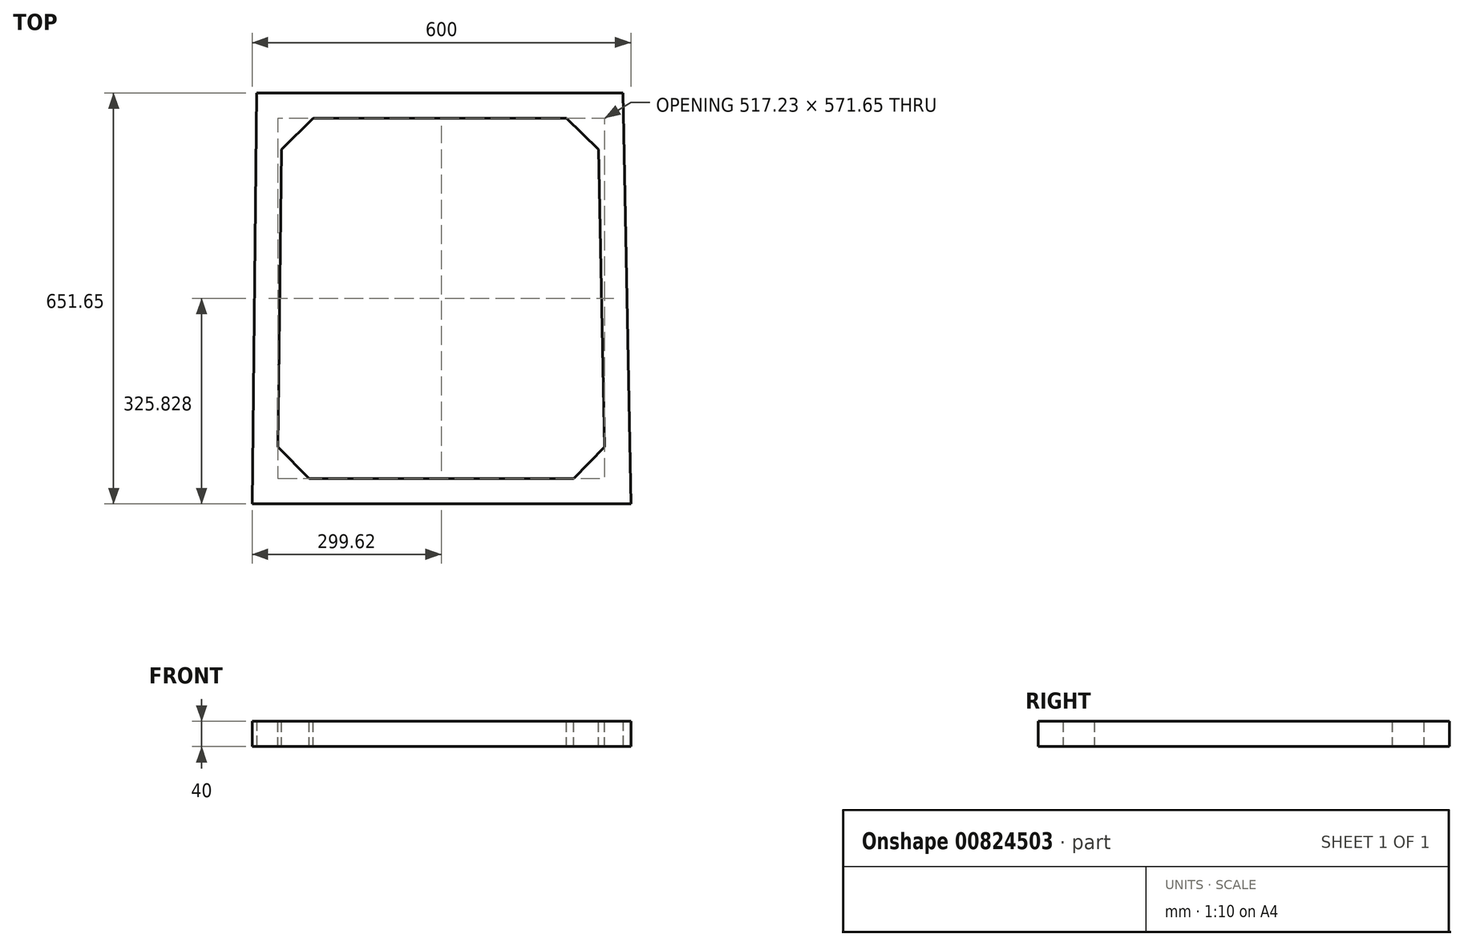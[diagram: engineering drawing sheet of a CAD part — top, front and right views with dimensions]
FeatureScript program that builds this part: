
annotation { "Feature Type Name" : "Feature", "Feature Type Description" : "" }
export const myFeature = defineFeature(function(context is Context, id is Id, definition is map)
    precondition{}
    {
        {
            var Q0;
            Q0=qCreatedBy(makeId("Top.planeOp"),FACE);
            var sketch = newSketch(context, id + "F0", { "sketchPlane" : qUnion([Q0])});
            skLineSegment(sketch, "E0.top", {"start": v(319.32, 303.94) * mm, "end": v(-260.68, 303.94) * mm});
            skLineSegment(sketch, "E1", {"start": v(-260.68, 303.94) * mm, "end": v(-267.92, -347.7) * mm});
            skLineSegment(sketch, "E2", {"start": v(319.32, 303.94) * mm, "end": v(332.08, -347.7) * mm});
            skLineSegment(sketch, "E3", {"start": v(332.08, -347.7) * mm, "end": v(-267.92, -347.7) * mm});
            skLineSegment(sketch, "E4.0", {"start": v(280.1, 263.94) * mm, "end": v(-221.12, 263.94) * mm});
            skLineSegment(sketch, "E4.1", {"start": v(280.1, 263.94) * mm, "end": v(291.3, -307.7) * mm});
            skLineSegment(sketch, "E4.2", {"start": v(291.3, -307.7) * mm, "end": v(-227.47, -307.7) * mm});
            skLineSegment(sketch, "E4.3", {"start": v(-221.12, 263.94) * mm, "end": v(-227.47, -307.7) * mm});
            skSolve(sketch);
        }
        {
            var Q0;
            Q0 = qSketchRegion(id + "F0", true);
            extrude(context, id + "F1", {"entities" : qUnion([Q0]), "depth" : 40 * mm, "offsetDistance" : 25 * mm});
        }
        {
            var Q0;
            Q0=makeQuery(id+"F1.opExtrude","CAP_FACE",FACE,{"disambiguationData":[OSD([sQuery(id+"F0.wireOp",EDGE,"E0.top"),sQuery(id+"F0.wireOp",EDGE,"E1"),sQuery(id+"F0.wireOp",EDGE,"E2"),sQuery(id+"F0.wireOp",EDGE,"E3"),sQuery(id+"F0.wireOp",EDGE,"E4.0"),sQuery(id+"F0.wireOp",EDGE,"E4.1"),sQuery(id+"F0.wireOp",EDGE,"E4.2"),sQuery(id+"F0.wireOp",EDGE,"E4.3")])],"isStart":false});
            var sketch = newSketch(context, id + "F2", { "sketchPlane" : qUnion([Q0])});
            skLineSegment(sketch, "E5", {"start": v(-221.12, 263.94) * mm, "end": v(-221.68, 213.94) * mm});
            skLineSegment(sketch, "E6", {"start": v(-221.68, 213.94) * mm, "end": v(-171.12, 263.94) * mm});
            skLineSegment(sketch, "E7", {"start": v(-171.12, 263.94) * mm, "end": v(-221.12, 263.94) * mm});
            skLineSegment(sketch, "E8", {"start": v(280.1, 263.94) * mm, "end": v(230.1, 263.94) * mm});
            skLineSegment(sketch, "E9", {"start": v(230.1, 263.94) * mm, "end": v(281.08, 213.95) * mm});
            skLineSegment(sketch, "E10", {"start": v(281.08, 213.95) * mm, "end": v(280.1, 263.94) * mm});
            skLineSegment(sketch, "E11", {"start": v(-227.47, -307.7) * mm, "end": v(-177.47, -307.7) * mm});
            skLineSegment(sketch, "E12", {"start": v(-177.47, -307.7) * mm, "end": v(-226.91, -257.7) * mm});
            skLineSegment(sketch, "E13", {"start": v(-226.91, -257.7) * mm, "end": v(-227.47, -307.7) * mm});
            skLineSegment(sketch, "E14", {"start": v(291.3, -307.7) * mm, "end": v(241.3, -307.7) * mm});
            skLineSegment(sketch, "E15", {"start": v(241.3, -307.7) * mm, "end": v(290.31, -257.71) * mm});
            skLineSegment(sketch, "E16", {"start": v(290.31, -257.71) * mm, "end": v(291.3, -307.7) * mm});
            skSolve(sketch);
        }
        {
            var Q0;
            Q0 = qSketchRegion(id + "F2", true);
            extrude(context, id + "F3", {"entities" : qUnion([Q0]), "operationType" : NewBodyOperationType.ADD, "oppositeDirection" : true, "depth" : 40 * mm, "offsetDistance" : 25 * mm});
        }
    });
